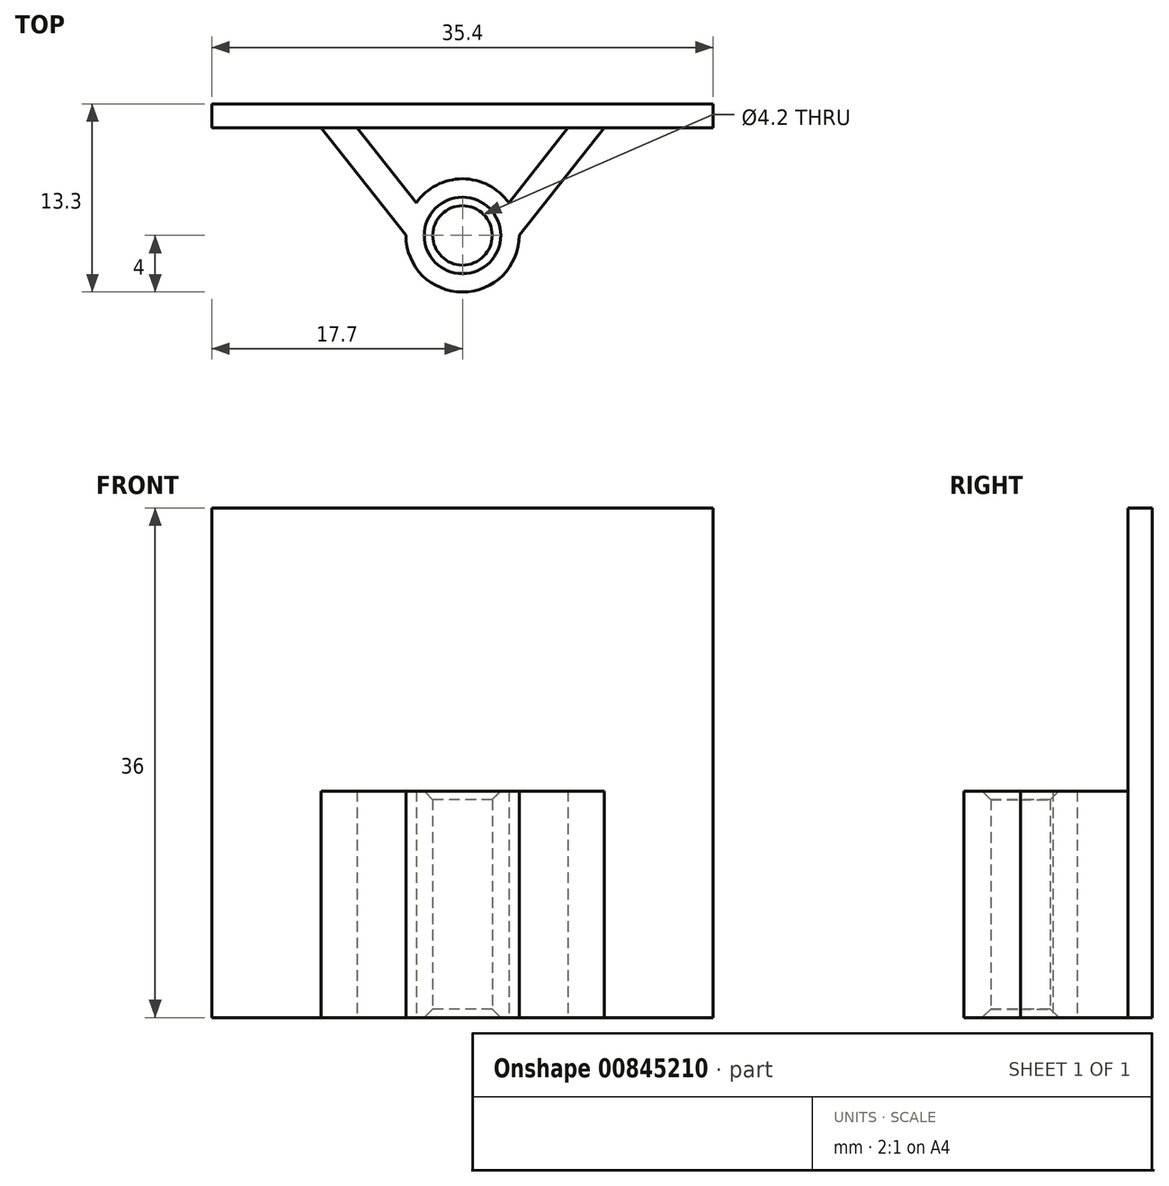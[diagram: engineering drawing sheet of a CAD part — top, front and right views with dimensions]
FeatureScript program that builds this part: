
annotation { "Feature Type Name" : "Feature", "Feature Type Description" : "" }
export const myFeature = defineFeature(function(context is Context, id is Id, definition is map)
    precondition{}
    {
        {
            var Q0;
            Q0=qCreatedBy(makeId("Top.planeOp"),FACE);
            var sketch = newSketch(context, id + "F0", { "sketchPlane" : qUnion([Q0])});
            skCircle(sketch, "E0", {"center": v(0, -8.45) * mm, "radius": 2.1 * mm});
            skLineSegment(sketch, "E1.bottom", {"start": v(-17.7, 0.85) * mm, "end": v(17.7, 0.85) * mm});
            skLineSegment(sketch, "E1.top", {"start": v(-17.7, -0.85) * mm, "end": v(17.7, -0.85) * mm});
            skLineSegment(sketch, "E1.left", {"start": v(-17.7, 0.85) * mm, "end": v(-17.7, -0.85) * mm});
            skLineSegment(sketch, "E1.right", {"start": v(17.7, 0.85) * mm, "end": v(17.7, -0.85) * mm});
            skPoint(sketch, "E1.middle", {"position": v(0, 0) * mm});
            skCircle(sketch, "E2", {"center": v(0, -8.45) * mm, "radius": 4 * mm});
            skLineSegment(sketch, "E3", {"start": v(0, -8.45) * mm, "end": v(4, -8.45) * mm, "construction": true});
            skLineSegment(sketch, "E4", {"start": v(0, -8.45) * mm, "end": v(-4, -8.45) * mm, "construction": true});
            skLineSegment(sketch, "E5", {"start": v(-4, -8.45) * mm, "end": v(-10, -0.85) * mm});
            skLineSegment(sketch, "E6", {"start": v(4, -8.45) * mm, "end": v(10, -0.85) * mm});
            skLineSegment(sketch, "E7", {"start": v(-1.99, -7.77) * mm, "end": v(-7.45, -0.85) * mm});
            skLineSegment(sketch, "E8", {"start": v(1.99, -7.77) * mm, "end": v(7.45, -0.85) * mm});
            skSolve(sketch);
        }
        {
            var Q0;
            Q0=makeQuery(id+"F0.imprint","IMPRINT",FACE,{"disambiguationData":[TD([[makeQuery(id+"F0.imprint","IMPRINT",EDGE,{"derivedFrom":sQuery(id+"F0.wireOp",EDGE,"E1.bottom")}),-1.0]])]});
            extrude(context, id + "F1", {"entities" : qUnion([Q0]), "depth" : 36 * mm, "offsetDistance" : 25 * mm});
        }
        {
            var Q0;
            {var subQ0=sQuery(id+"F0.wireOp",EDGE,"E5");Q0=makeQuery(id+"F0.imprint","IMPRINT",FACE,{"disambiguationData":[TD([[makeQuery(id+"F0.imprint","IMPRINT",EDGE,{"derivedFrom":subQ0}),-1.0]])]});}
            var Q1;
            {var subQ0=sQuery(id+"F0.wireOp",EDGE,"E6");Q1=makeQuery(id+"F0.imprint","IMPRINT",FACE,{"disambiguationData":[TD([[makeQuery(id+"F0.imprint","IMPRINT",EDGE,{"derivedFrom":subQ0}),1.0]])]});}
            var Q2;
            {var subQ3=sQuery(id+"F0.wireOp",EDGE,"E7");var subQ5=sQuery(id+"F0.wireOp",EDGE,"E0");var subQ6=makeQuery(id+"F0.imprint","INTERSECT",VERTEX,{"derivedFrom":[subQ5,subQ3]});Q2=makeQuery(id+"F0.imprint","IMPRINT",FACE,{"disambiguationData":[TD([[makeQuery(id+"F0.imprint","IMPRINT",EDGE,{"disambiguationData":[TD([[subQ6,-1.0]])],"derivedFrom":subQ5}),-1.0]])]});}
            var Q3;
            {var subQ0=sQuery(id+"F0.wireOp",EDGE,"E7");var subQ1=sQuery(id+"F0.wireOp",EDGE,"E0");var subQ2=makeQuery(id+"F0.imprint","INTERSECT",VERTEX,{"derivedFrom":[subQ1,subQ0]});Q3=makeQuery(id+"F0.imprint","IMPRINT",FACE,{"disambiguationData":[TD([[makeQuery(id+"F0.imprint","IMPRINT",EDGE,{"disambiguationData":[TD([[subQ2,1.0]])],"derivedFrom":subQ1}),-1.0]])]});}
            extrude(context, id + "F2", {"entities" : qUnion([Q0, Q1, Q2, Q3]), "operationType" : NewBodyOperationType.ADD, "depth" : 16 * mm, "offsetDistance" : 25 * mm});
        }
        {
            var Q0;
            Q0=makeQuery(id+"F2.opExtrude","CAP_EDGE",EDGE,{"disambiguationData":[OSD([sQuery(id+"F0.wireOp",EDGE,"E0")])],"isStart":true});
            var Q1;
            Q1=makeQuery(id+"F2.opExtrude","CAP_EDGE",EDGE,{"disambiguationData":[OSD([sQuery(id+"F0.wireOp",EDGE,"E0")])],"isStart":false});
            chamfer(context, id + "F3", {"entities" : qUnion([Q0, Q1]), "width" : .6 * mm, "tangentPropagation" : true});
        }
    });
